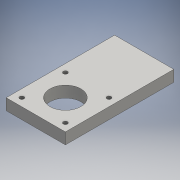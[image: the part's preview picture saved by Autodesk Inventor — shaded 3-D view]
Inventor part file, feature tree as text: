
AUTODESK INVENTOR PART (.ipt)
format: ipt  version: 2016 SP1 (Build 200210100, 210)  size: 111,104 bytes
history: native  units: mm
features: extrude x2, sketch x2, projected_geometry x1
ambient origin geometry x8: Origin, YZ Plane, XZ Plane, XY Plane, X Axis, Y Axis, Z Axis, Center Point
bodies: Solid1 (feature_tree)
feature tree (5):
  extrude  "Extrusion1"  Depth=8.0mm TaperAngle=0.0deg
  extrude  "Extrusion2"  [1 undecoded]
  sketch  "Sketch1"  dims[d0=8.0mm d1=0.0mm d2=35.0mm d3=0.0mm]
  sketch  "Sketch2"
  projected_geometry  "Projected Loop1"
note: 1 required parameter value undecoded (feature->parameter linkage not recoverable at this tier; creation-order binding heuristic only, values carry confidence <= 0.55)
